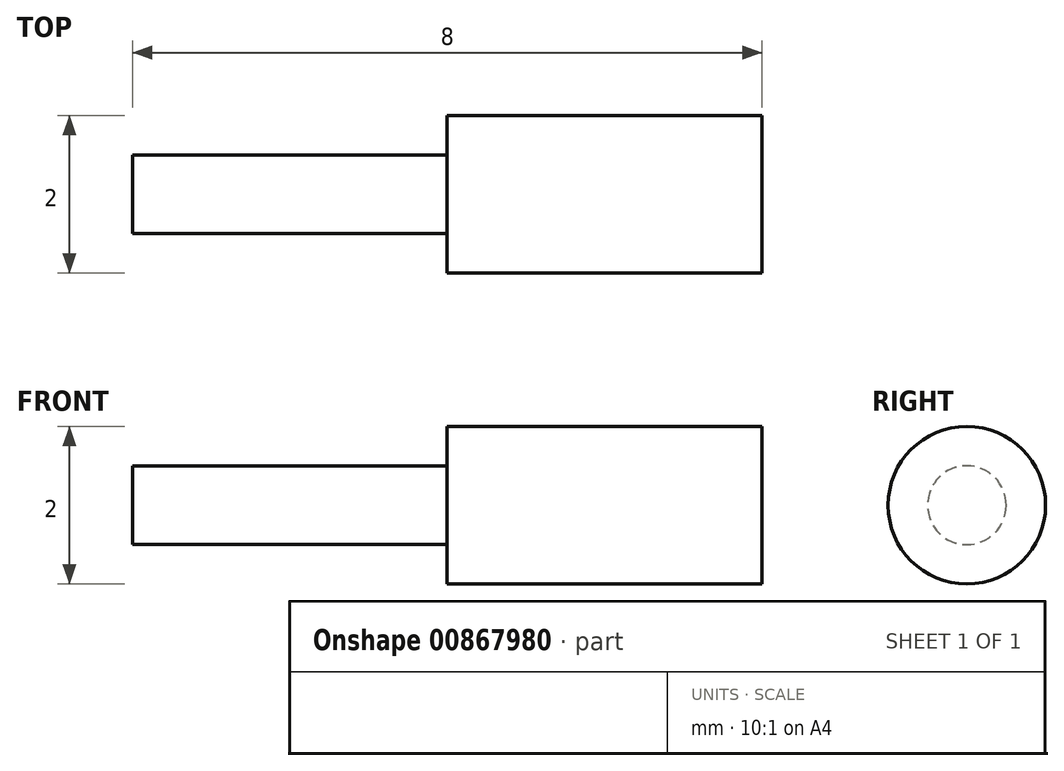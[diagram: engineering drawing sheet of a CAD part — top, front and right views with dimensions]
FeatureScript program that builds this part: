
annotation { "Feature Type Name" : "Feature", "Feature Type Description" : "" }
export const myFeature = defineFeature(function(context is Context, id is Id, definition is map)
    precondition{}
    {
        {
            var Q0;
            Q0=qCreatedBy(makeId("Front.planeOp"),FACE);
            var sketch = newSketch(context, id + "F0", { "sketchPlane" : qUnion([Q0])});
            skLineSegment(sketch, "E0", {"start": v(-8, 0) * mm, "end": v(-8, 0.5) * mm});
            skLineSegment(sketch, "E1", {"start": v(-8, 0.5) * mm, "end": v(-4, 0.5) * mm});
            skLineSegment(sketch, "E2", {"start": v(-4, 0.5) * mm, "end": v(-4, 1) * mm});
            skLineSegment(sketch, "E3", {"start": v(-4, 1) * mm, "end": v(0, 1) * mm});
            skLineSegment(sketch, "E4", {"start": v(0, 1) * mm, "end": v(0, 0) * mm});
            skLineSegment(sketch, "E5", {"start": v(0, 0) * mm, "end": v(-8, 0) * mm});
            skSolve(sketch);
        }
        {
            var Q0;
            Q0 = qSketchRegion(id + "F0", true);
            var Q1;
            Q1=sQuery(id+"F0.wireOp",EDGE,"E5");
            revolve(context, id + "F1", {"surfaceOperationType" : NewSurfaceOperationType.NEW, "entities" : qUnion([Q0]), "axis" : qUnion([Q1]), "revolveType" : RevolveType.FULL});
        }
    });
